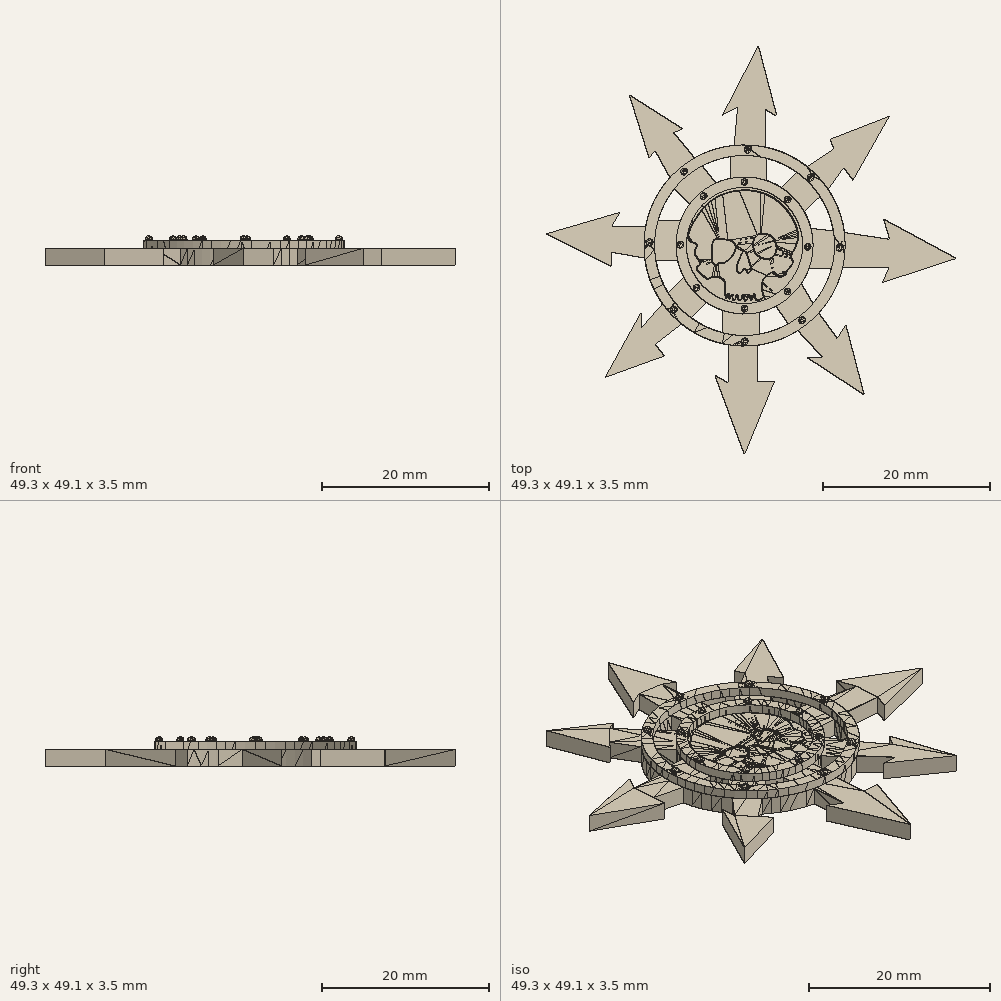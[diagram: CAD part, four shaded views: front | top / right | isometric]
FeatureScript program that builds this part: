
annotation { "Feature Type Name" : "Feature", "Feature Type Description" : "" }
export const myFeature = defineFeature(function(context is Context, id is Id, definition is map)
    precondition{}
    {
        {
            var Q0;
            Q0=qCreatedBy(makeId("Top.planeOp"),FACE);
            var sketch = newSketch(context, id + "F0", { "sketchPlane" : qUnion([Q0])});
            skLineSegment(sketch, "E0", {"start": v(0, -16.17) * mm, "end": v(-3.58, -6.6) * mm});
            skLineSegment(sketch, "E1", {"start": v(-3.58, -6.6) * mm, "end": v(-1.93, -7.54) * mm});
            skLineSegment(sketch, "E2", {"start": v(-1.93, -2.96) * mm, "end": v(-1.93, -2.93) * mm});
            skLineSegment(sketch, "E3", {"start": v(0, -16.17) * mm, "end": v(3.63, -7.3) * mm});
            skLineSegment(sketch, "E4", {"start": v(3.63, -7.3) * mm, "end": v(1.58, -7.3) * mm});
            skLineSegment(sketch, "E5", {"start": v(14.38, -8.95) * mm, "end": v(7.48, -4.44) * mm});
            skLineSegment(sketch, "E6", {"start": v(7.48, -4.44) * mm, "end": v(9.38, -4.44) * mm});
            skLineSegment(sketch, "E7", {"start": v(14.38, -8.95) * mm, "end": v(12.2, -0.6) * mm});
            skLineSegment(sketch, "E8", {"start": v(12.2, -0.6) * mm, "end": v(11.15, -2.18) * mm});
            skLineSegment(sketch, "E9", {"start": v(25.47, 7.44) * mm, "end": v(16.6, 4.54) * mm});
            skLineSegment(sketch, "E10", {"start": v(16.6, 4.54) * mm, "end": v(17.37, 6.37) * mm});
            skLineSegment(sketch, "E11", {"start": v(25.47, 7.44) * mm, "end": v(16.72, 12.17) * mm});
            skLineSegment(sketch, "E12", {"start": v(16.72, 12.17) * mm, "end": v(17.43, 9.74) * mm});
            skLineSegment(sketch, "E13", {"start": v(12.01, 10.56) * mm, "end": v(11.93, 10.57) * mm});
            skLineSegment(sketch, "E14", {"start": v(11.93, 18.31) * mm, "end": v(13.06, 16.84) * mm});
            skLineSegment(sketch, "E15", {"start": v(13.06, 16.84) * mm, "end": v(17.43, 24.52) * mm});
            skLineSegment(sketch, "E16", {"start": v(17.43, 24.52) * mm, "end": v(10.28, 21.74) * mm});
            skLineSegment(sketch, "E17", {"start": v(10.28, 21.74) * mm, "end": v(10.74, 20.55) * mm});
            skCircle(sketch, "E18", {"center": v(0, 9) * mm, "radius": 6.99 * mm});
            skArc(sketch, "E19", {"start": v(-6.58, 14) * mm, "mid": v(-7.21, 13.01) * mm, "end": v(-7.7, 11.95) * mm});
            skArc(sketch, "E20", {"start": v(-8.42, 15.76) * mm, "mid": v(-9.6, 13.96) * mm, "end": v(-10.38, 11.95) * mm});
            skArc(sketch, "E21", {"start": v(-1.24, 21.05) * mm, "mid": v(-3.7, 20.53) * mm, "end": v(-6, 19.52) * mm});
            skLineSegment(sketch, "E22", {"start": v(10.74, 20.55) * mm, "end": v(7.55, 18.47) * mm});
            skLineSegment(sketch, "E23", {"start": v(11.93, 18.31) * mm, "end": v(10.07, 15.73) * mm});
            skLineSegment(sketch, "E24", {"start": v(17.43, 9.74) * mm, "end": v(12.01, 10.56) * mm});
            skLineSegment(sketch, "E25", {"start": v(17.37, 6.37) * mm, "end": v(11.82, 6.37) * mm});
            skLineSegment(sketch, "E26", {"start": v(11.15, -2.18) * mm, "end": v(8.95, 0.84) * mm});
            skLineSegment(sketch, "E27", {"start": v(9.38, -4.44) * mm, "end": v(6.43, -1.26) * mm});
            skLineSegment(sketch, "E28", {"start": v(1.58, -7.3) * mm, "end": v(1.58, -3) * mm});
            skLineSegment(sketch, "E29", {"start": v(-1.93, -7.54) * mm, "end": v(-1.93, -2.96) * mm});
            skLineSegment(sketch, "E30", {"start": v(-9.85, 1.95) * mm, "end": v(-12.42, -0.96) * mm});
            skLineSegment(sketch, "E31", {"start": v(-12.42, -0.96) * mm, "end": v(-12.42, 0.93) * mm});
            skLineSegment(sketch, "E32", {"start": v(-12.42, 0.93) * mm, "end": v(-16.74, -6.87) * mm});
            skLineSegment(sketch, "E33", {"start": v(-16.74, -6.87) * mm, "end": v(-9.63, -4.3) * mm});
            skLineSegment(sketch, "E34", {"start": v(-9.63, -4.3) * mm, "end": v(-10.7, -2.92) * mm});
            skLineSegment(sketch, "E35", {"start": v(-10.7, -2.92) * mm, "end": v(-7.57, -0.46) * mm});
            skLineSegment(sketch, "E36", {"start": v(-12.02, 7.5) * mm, "end": v(-15.95, 8.18) * mm});
            skLineSegment(sketch, "E37", {"start": v(-15.95, 8.18) * mm, "end": v(-15.95, 6.43) * mm});
            skLineSegment(sketch, "E38", {"start": v(-15.95, 6.43) * mm, "end": v(-23.8, 10.4) * mm});
            skLineSegment(sketch, "E39", {"start": v(-23.8, 10.4) * mm, "end": v(-14.94, 12.98) * mm});
            skLineSegment(sketch, "E40", {"start": v(-14.94, 12.98) * mm, "end": v(-15.98, 11.23) * mm});
            skLineSegment(sketch, "E41", {"start": v(-15.98, 11.23) * mm, "end": v(-11.9, 11.23) * mm});
            skLineSegment(sketch, "E42", {"start": v(-8.97, 17.14) * mm, "end": v(-10.73, 20.34) * mm});
            skLineSegment(sketch, "E43", {"start": v(-10.73, 20.34) * mm, "end": v(-11.47, 19.5) * mm});
            skLineSegment(sketch, "E44", {"start": v(-11.47, 19.5) * mm, "end": v(-13.86, 27.1) * mm});
            skLineSegment(sketch, "E45", {"start": v(-13.86, 27.1) * mm, "end": v(-7.45, 23.03) * mm});
            skLineSegment(sketch, "E46", {"start": v(-7.45, 23.03) * mm, "end": v(-8.49, 22.53) * mm});
            skLineSegment(sketch, "E47", {"start": v(-8.49, 22.53) * mm, "end": v(-6, 19.52) * mm});
            skLineSegment(sketch, "E48", {"start": v(-1.24, 21.05) * mm, "end": v(-0.83, 25.6) * mm});
            skLineSegment(sketch, "E49", {"start": v(-0.83, 25.6) * mm, "end": v(-2.62, 24.67) * mm});
            skLineSegment(sketch, "E50", {"start": v(-2.62, 24.67) * mm, "end": v(1.67, 32.98) * mm});
            skLineSegment(sketch, "E51", {"start": v(1.67, 32.98) * mm, "end": v(3.89, 24.53) * mm});
            skLineSegment(sketch, "E52", {"start": v(3.89, 24.53) * mm, "end": v(2.52, 25.33) * mm});
            skLineSegment(sketch, "E53", {"start": v(2.52, 25.33) * mm, "end": v(2.52, 20.85) * mm});
            skArc(sketch, "E54.trimOffspring", {"start": v(-8.97, 17.14) * mm, "mid": v(-10.85, 14.4) * mm, "end": v(-11.9, 11.23) * mm});
            skArc(sketch, "E55.trimOffspring", {"start": v(7.55, 18.47) * mm, "mid": v(5.17, 19.95) * mm, "end": v(2.52, 20.85) * mm});
            skArc(sketch, "E56.trimOffspring", {"start": v(12.01, 10.56) * mm, "mid": v(11.34, 13.26) * mm, "end": v(10.07, 15.73) * mm});
            skArc(sketch, "E57.trimOffspring", {"start": v(-12.02, 7.5) * mm, "mid": v(-11.28, 4.59) * mm, "end": v(-9.85, 1.95) * mm});
            skArc(sketch, "E58.trimOffspring", {"start": v(8.95, 0.84) * mm, "mid": v(10.75, 3.42) * mm, "end": v(11.82, 6.37) * mm});
            skArc(sketch, "E59.trimOffspring", {"start": v(1.58, -3) * mm, "mid": v(4.1, -2.4) * mm, "end": v(6.43, -1.26) * mm});
            skArc(sketch, "E60.trimOffspring", {"start": v(-7.57, -0.46) * mm, "mid": v(-4.9, -2.07) * mm, "end": v(-1.93, -2.96) * mm});
            skLineSegment(sketch, "E61", {"start": v(-1.64, 19.67) * mm, "end": v(-1.64, 17.1) * mm});
            skLineSegment(sketch, "E62", {"start": v(2.69, 19.46) * mm, "end": v(2.69, 16.8) * mm});
            skLineSegment(sketch, "E63", {"start": v(6.26, 17.8) * mm, "end": v(4.47, 15.94) * mm});
            skLineSegment(sketch, "E64", {"start": v(9.08, 14.83) * mm, "end": v(7.19, 13.06) * mm});
            skLineSegment(sketch, "E65", {"start": v(10.65, 10.75) * mm, "end": v(8, 11.06) * mm});
            skLineSegment(sketch, "E66", {"start": v(10.44, 6.24) * mm, "end": v(7.78, 6.24) * mm});
            skLineSegment(sketch, "E67", {"start": v(8.24, 2.02) * mm, "end": v(6.84, 4.37) * mm});
            skLineSegment(sketch, "E68", {"start": v(5.25, -0.43) * mm, "end": v(3.8, 1.67) * mm});
            skLineSegment(sketch, "E69", {"start": v(1.82, -1.64) * mm, "end": v(1.82, 0.95) * mm});
            skLineSegment(sketch, "E70", {"start": v(-2.6, -1.48) * mm, "end": v(-2.6, 1.17) * mm});
            skLineSegment(sketch, "E71", {"start": v(-6.4, 0.3) * mm, "end": v(-4.52, 2.1) * mm});
            skLineSegment(sketch, "E72", {"start": v(-9.17, 3.3) * mm, "end": v(-7.3, 5.14) * mm});
            skLineSegment(sketch, "E73", {"start": v(-10.64, 7.16) * mm, "end": v(-8.05, 7.16) * mm});
            skLineSegment(sketch, "E74", {"start": v(-10.38, 11.95) * mm, "end": v(-7.7, 11.95) * mm});
            skLineSegment(sketch, "E75", {"start": v(-8.42, 15.76) * mm, "end": v(-6.58, 14) * mm});
            skLineSegment(sketch, "E76", {"start": v(-5.07, 18.53) * mm, "end": v(-3.44, 16.5) * mm});
            skArc(sketch, "E77.trimOffspring", {"start": v(-8.05, 7.16) * mm, "mid": v(-7.74, 6.13) * mm, "end": v(-7.3, 5.14) * mm});
            skArc(sketch, "E78.trimOffspring", {"start": v(-4.52, 2.1) * mm, "mid": v(-3.6, 1.57) * mm, "end": v(-2.6, 1.17) * mm});
            skArc(sketch, "E79.trimOffspring", {"start": v(-6.4, 0.3) * mm, "mid": v(-4.59, -0.77) * mm, "end": v(-2.6, -1.48) * mm});
            skArc(sketch, "E80.trimOffspring", {"start": v(-10.64, 7.16) * mm, "mid": v(-10.09, 5.16) * mm, "end": v(-9.17, 3.3) * mm});
            skArc(sketch, "E81.trimOffspring", {"start": v(-1.64, 19.67) * mm, "mid": v(-3.4, 19.25) * mm, "end": v(-5.07, 18.53) * mm});
            skArc(sketch, "E82.trimOffspring", {"start": v(-1.64, 17.1) * mm, "mid": v(-2.56, 16.85) * mm, "end": v(-3.44, 16.5) * mm});
            skArc(sketch, "E83.trimOffspring", {"start": v(4.47, 15.94) * mm, "mid": v(3.6, 16.43) * mm, "end": v(2.69, 16.8) * mm});
            skArc(sketch, "E84.trimOffspring", {"start": v(6.26, 17.8) * mm, "mid": v(4.55, 18.8) * mm, "end": v(2.69, 19.46) * mm});
            skArc(sketch, "E85.trimOffspring", {"start": v(10.65, 10.75) * mm, "mid": v(10.08, 12.87) * mm, "end": v(9.08, 14.83) * mm});
            skArc(sketch, "E86.trimOffspring", {"start": v(8, 11.06) * mm, "mid": v(7.66, 12.09) * mm, "end": v(7.19, 13.06) * mm});
            skArc(sketch, "E87.trimOffspring", {"start": v(8.24, 2.02) * mm, "mid": v(9.57, 4) * mm, "end": v(10.44, 6.24) * mm});
            skArc(sketch, "E88.trimOffspring", {"start": v(6.84, 4.37) * mm, "mid": v(7.37, 5.28) * mm, "end": v(7.78, 6.24) * mm});
            skArc(sketch, "E89.trimOffspring", {"start": v(1.82, 0.95) * mm, "mid": v(2.83, 1.25) * mm, "end": v(3.8, 1.67) * mm});
            skArc(sketch, "E90.trimOffspring", {"start": v(1.82, -1.64) * mm, "mid": v(3.59, -1.18) * mm, "end": v(5.25, -0.43) * mm});
            skCircle(sketch, "E91", {"center": v(0, 9) * mm, "radius": 8.24 * mm});
            skCircle(sketch, "E92", {"center": v(0, 9) * mm, "radius": 12.1 * mm});
            skCircle(sketch, "E93", {"center": v(0, 9) * mm, "radius": 10.82 * mm});
            skSolve(sketch);
        }
        {
            var Q0;
            Q0 = qSketchRegion(id + "F0", true);
            extrude(context, id + "F1", {"entities" : qUnion([Q0]), "depth" : 2 * mm});
        }
        {
            var Q0;
            Q0=makeQuery(id+"F0.imprint","IMPRINT",FACE,{"disambiguationData":[TD([[makeQuery(id+"F0.imprint","IMPRINT",EDGE,{"derivedFrom":sQuery(id+"F0.wireOp",EDGE,"E18")}),1.0]])]});
            extrude(context, id + "F2", {"entities" : qUnion([Q0]), "operationType" : NewBodyOperationType.ADD, "depth" : 2 * mm});
        }
        {
            var Q0;
            Q0=makeQuery(id+"F0.imprint","IMPRINT",FACE,{"disambiguationData":[TD([[makeQuery(id+"F0.imprint","IMPRINT",EDGE,{"derivedFrom":sQuery(id+"F0.wireOp",EDGE,"E19")}),1.0]])]});
            extrude(context, id + "F3", {"entities" : qUnion([Q0]), "operationType" : NewBodyOperationType.ADD, "depth" : 2 * mm});
        }
        {
            var Q0;
            Q0=makeQuery(id+"F0.imprint","IMPRINT",FACE,{"disambiguationData":[TD([[makeQuery(id+"F0.imprint","IMPRINT",EDGE,{"derivedFrom":sQuery(id+"F0.wireOp",EDGE,"E18")}),-1.0]])]});
            var Q1;
            Q1=makeQuery(id+"F0.imprint","IMPRINT",FACE,{"disambiguationData":[TD([[makeQuery(id+"F0.imprint","IMPRINT",EDGE,{"derivedFrom":sQuery(id+"F0.wireOp",EDGE,"E93")}),-1.0]])]});
            extrude(context, id + "F4", {"entities" : qUnion([Q0, Q1]), "depth" : 3 * mm});
        }
        {
            var Q0;
            Q0=makeQuery(id+"F2.opExtrude","CAP_FACE",FACE,{"disambiguationData":[OSD([sQuery(id+"F0.wireOp",EDGE,"E18")])],"isStart":false});
            var sketch = newSketch(context, id + "F5", { "sketchPlane" : qUnion([Q0])});
            skFitSpline(sketch, "E94", {"points": [v(-3.63, 9.6) * mm, v(-2.74, 9.72) * mm, v(-1.66, 9.54) * mm, v(-1.14, 8.98) * mm, v(-1.26, 8.15) * mm, v(-1.72, 7.5) * mm, v(-2.62, 6.92) * mm, v(-3.14, 6.92) * mm, v(-3.26, 6.67) * mm, v(-3.76, 6.92) * mm, v(-3.88, 7.72) * mm, v(-3.63, 9.6) * mm]});
            skFitSpline(sketch, "E95", {"points": [v(1.51, 10.16) * mm, v(2.68, 10.3) * mm, v(3.58, 9.6) * mm, v(3.7, 8.12) * mm, v(2.96, 7.44) * mm, v(1.64, 7.81) * mm, v(1.08, 8.95) * mm, v(1.51, 10.16) * mm]});
            skFitSpline(sketch, "E96", {"points": [v(-0.46, 5.75) * mm, v(-0.86, 5.96) * mm, v(-0.74, 6.92) * mm, v(-0.37, 7.78) * mm, v(0, 8.24) * mm, v(0.5, 7.17) * mm, v(0.71, 5.96) * mm, v(0.43, 5.78) * mm, v(0, 6.3) * mm, v(-0.46, 5.75) * mm]});
            skFitSpline(sketch, "E97", {"points": [v(-4.46, 4.87) * mm, v(-3.63, 5.17) * mm, v(-2.62, 4.87) * mm, v(-2.38, 4.31) * mm, v(-2.4, 3.38) * mm, v(-2.14, 2.6) * mm, v(-1.96, 3.14) * mm, v(-1.8, 2.53) * mm, v(-1.48, 3.06) * mm, v(-1.47, 2.55) * mm, v(-1.11, 2.46) * mm, v(-0.9, 3.04) * mm, v(-0.74, 2.43) * mm, v(-0.37, 2.46) * mm, v(-0.2, 3.06) * mm, v(0, 2.35) * mm, v(0.35, 2.44) * mm, v(0.51, 3.04) * mm, v(0.83, 2.35) * mm, v(1.17, 3.09) * mm, v(1.37, 2.45) * mm, v(2.3, 2.72) * mm, v(2.27, 3.14) * mm, v(2.22, 4.68) * mm, v(3.3, 5.7) * mm], "startDerivative": vector(16.77, 9.14) * mm, "endDerivative": vector(23.15, 14.13) * mm});
            skFitSpline(sketch, "E98", {"points": [v(3.3, 5.7) * mm, v(3.55, 5.7) * mm, v(4.1, 5.2) * mm, v(4.99, 5.46) * mm, v(5.05, 5.7) * mm, v(5.87, 6.97) * mm, v(5.64, 7.55) * mm, v(6.46, 9.68) * mm, v(4.43, 14.02) * mm, v(0.42, 15.69) * mm, v(-3.37, 14.8) * mm, v(-5.85, 12.29) * mm, v(-6.7, 9.61) * mm, v(-5.75, 9.06) * mm, v(-6.05, 8.1) * mm, v(-5.36, 6.84) * mm, v(-5.79, 6.35) * mm, v(-4.46, 4.87) * mm], "startDerivative": vector(10.94, 3.43) * mm, "endDerivative": vector(33.26, -26.4) * mm});
            skSolve(sketch);
        }
        {
            var Q0;
            Q0=makeQuery(id+"F5.imprint","IMPRINT",FACE,{"disambiguationData":[TD([[makeQuery(id+"F5.imprint","IMPRINT",EDGE,{"derivedFrom":sQuery(id+"F5.wireOp",EDGE,"E94")}),1.0]])]});
            extrude(context, id + "F6", {"entities" : qUnion([Q0]), "operationType" : NewBodyOperationType.ADD, "depth" : .2 * mm});
        }
        {
            var Q0;
            Q0=makeQuery(id+"F6.opExtrude","CAP_EDGE",EDGE,{"disambiguationData":[OSD([sQuery(id+"F5.wireOp",EDGE,"E94")])],"isStart":false});
            fillet(context, id + "F7", {"entities" : qUnion([Q0]), "radius" : .1 * mm, "tangentPropagation" : true, "allowEdgeOverflow" : false});
        }
        {
            var Q0;
            Q0=makeQuery(id+"F6.opExtrude","CAP_EDGE",EDGE,{"disambiguationData":[OSD([sQuery(id+"F5.wireOp",EDGE,"E95")])],"isStart":false});
            var Q1;
            Q1=makeQuery(id+"F6.opExtrude","CAP_FACE",FACE,{"disambiguationData":[OSD([sQuery(id+"F5.wireOp",EDGE,"E94"),sQuery(id+"F5.wireOp",EDGE,"E95"),sQuery(id+"F5.wireOp",EDGE,"E96"),sQuery(id+"F5.wireOp",EDGE,"E97"),sQuery(id+"F5.wireOp",EDGE,"E98")])],"isStart":false});
            fillet(context, id + "F8", {"entities" : qUnion([Q0, Q1]), "radius" : .1 * mm, "tangentPropagation" : true, "allowEdgeOverflow" : false});
        }
        {
            var Q0;
            Q0=makeQuery(id+"F4.opExtrude","CAP_FACE",FACE,{"disambiguationData":[OSD([sQuery(id+"F0.wireOp",EDGE,"E92"),sQuery(id+"F0.wireOp",EDGE,"E93")])],"isStart":false});
            var sketch = newSketch(context, id + "F9", { "sketchPlane" : qUnion([Q0])});
            skCircle(sketch, "E99", {"center": v(-11.4, 9.38) * mm, "radius": 0.42 * mm});
            skCircle(sketch, "E100", {"center": v(-8.5, 1.27) * mm, "radius": 0.42 * mm});
            skCircle(sketch, "E101", {"center": v(0, -2.53) * mm, "radius": 0.42 * mm});
            skCircle(sketch, "E102", {"center": v(6.94, 0) * mm, "radius": 0.42 * mm});
            skCircle(sketch, "E103", {"center": v(11.44, 8.72) * mm, "radius": 0.42 * mm});
            skCircle(sketch, "E104", {"center": v(7.95, 17.16) * mm, "radius": 0.42 * mm});
            skCircle(sketch, "E105", {"center": v(0.4, 20.5) * mm, "radius": 0.42 * mm});
            skCircle(sketch, "E106", {"center": v(-7.22, 17.9) * mm, "radius": 0.42 * mm});
            skSolve(sketch);
        }
        {
            var Q0;
            Q0=makeQuery(id+"F9.imprint","IMPRINT",FACE,{"disambiguationData":[TD([[makeQuery(id+"F9.imprint","IMPRINT",EDGE,{"derivedFrom":sQuery(id+"F9.wireOp",EDGE,"E100")}),1.0]])]});
            var Q1;
            Q1=makeQuery(id+"F9.imprint","IMPRINT",FACE,{"disambiguationData":[TD([[makeQuery(id+"F9.imprint","IMPRINT",EDGE,{"derivedFrom":sQuery(id+"F9.wireOp",EDGE,"E101")}),1.0]])]});
            var Q2;
            Q2=makeQuery(id+"F9.imprint","IMPRINT",FACE,{"disambiguationData":[TD([[makeQuery(id+"F9.imprint","IMPRINT",EDGE,{"derivedFrom":sQuery(id+"F9.wireOp",EDGE,"E102")}),1.0]])]});
            var Q3;
            Q3=makeQuery(id+"F9.imprint","IMPRINT",FACE,{"disambiguationData":[TD([[makeQuery(id+"F9.imprint","IMPRINT",EDGE,{"derivedFrom":sQuery(id+"F9.wireOp",EDGE,"E103")}),1.0]])]});
            var Q4;
            Q4=makeQuery(id+"F9.imprint","IMPRINT",FACE,{"disambiguationData":[TD([[makeQuery(id+"F9.imprint","IMPRINT",EDGE,{"derivedFrom":sQuery(id+"F9.wireOp",EDGE,"E104")}),1.0]])]});
            var Q5;
            Q5=makeQuery(id+"F9.imprint","IMPRINT",FACE,{"disambiguationData":[TD([[makeQuery(id+"F9.imprint","IMPRINT",EDGE,{"derivedFrom":sQuery(id+"F9.wireOp",EDGE,"E105")}),1.0]])]});
            var Q6;
            Q6=makeQuery(id+"F9.imprint","IMPRINT",FACE,{"disambiguationData":[TD([[makeQuery(id+"F9.imprint","IMPRINT",EDGE,{"derivedFrom":sQuery(id+"F9.wireOp",EDGE,"E106")}),1.0]])]});
            var Q7;
            Q7=makeQuery(id+"F9.imprint","IMPRINT",FACE,{"disambiguationData":[TD([[makeQuery(id+"F9.imprint","IMPRINT",EDGE,{"derivedFrom":sQuery(id+"F9.wireOp",EDGE,"E99")}),1.0]])]});
            extrude(context, id + "F10", {"entities" : qUnion([Q0, Q1, Q2, Q3, Q4, Q5, Q6, Q7]), "operationType" : NewBodyOperationType.ADD, "depth" : .5 * mm});
        }
        {
            var Q0;
            Q0=makeQuery(id+"F10.opExtrude","CAP_EDGE",EDGE,{"disambiguationData":[OSD([sQuery(id+"F9.wireOp",EDGE,"E99")])],"isStart":false});
            fillet(context, id + "F11", {"entities" : qUnion([Q0]), "radius" : .4 * mm, "tangentPropagation" : true, "allowEdgeOverflow" : false});
        }
        {
            var Q0;
            Q0=makeQuery(id+"F10.opExtrude","CAP_EDGE",EDGE,{"disambiguationData":[OSD([sQuery(id+"F9.wireOp",EDGE,"E106")])],"isStart":false});
            var Q1;
            Q1=makeQuery(id+"F10.opExtrude","CAP_EDGE",EDGE,{"disambiguationData":[OSD([sQuery(id+"F9.wireOp",EDGE,"E100")])],"isStart":false});
            var Q2;
            Q2=makeQuery(id+"F10.opExtrude","CAP_EDGE",EDGE,{"disambiguationData":[OSD([sQuery(id+"F9.wireOp",EDGE,"E101")])],"isStart":false});
            var Q3;
            Q3=makeQuery(id+"F10.opExtrude","CAP_EDGE",EDGE,{"disambiguationData":[OSD([sQuery(id+"F9.wireOp",EDGE,"E102")])],"isStart":false});
            var Q4;
            Q4=makeQuery(id+"F10.opExtrude","CAP_EDGE",EDGE,{"disambiguationData":[OSD([sQuery(id+"F9.wireOp",EDGE,"E105")])],"isStart":false});
            var Q5;
            Q5=makeQuery(id+"F10.opExtrude","CAP_EDGE",EDGE,{"disambiguationData":[OSD([sQuery(id+"F9.wireOp",EDGE,"E104")])],"isStart":false});
            var Q6;
            Q6=makeQuery(id+"F10.opExtrude","CAP_EDGE",EDGE,{"disambiguationData":[OSD([sQuery(id+"F9.wireOp",EDGE,"E103")])],"isStart":false});
            fillet(context, id + "F12", {"entities" : qUnion([Q0, Q1, Q2, Q3, Q4, Q5, Q6]), "radius" : .4 * mm, "tangentPropagation" : true, "allowEdgeOverflow" : false});
        }
        {
            var Q0;
            Q0=makeQuery(id+"F4.opExtrude","CAP_FACE",FACE,{"disambiguationData":[OSD([sQuery(id+"F0.wireOp",EDGE,"E18"),sQuery(id+"F0.wireOp",EDGE,"E91")])],"isStart":false});
            var sketch = newSketch(context, id + "F13", { "sketchPlane" : qUnion([Q0])});
            skCircle(sketch, "E107", {"center": v(0, 16.63) * mm, "radius": 0.4 * mm});
            skCircle(sketch, "E108", {"center": v(5.2, 14.51) * mm, "radius": 0.4 * mm});
            skCircle(sketch, "E109", {"center": v(-4.9, 14.92) * mm, "radius": 0.4 * mm});
            skCircle(sketch, "E110", {"center": v(-7.7, 9.08) * mm, "radius": 0.4 * mm});
            skCircle(sketch, "E111", {"center": v(-5.76, 3.9) * mm, "radius": 0.4 * mm});
            skCircle(sketch, "E112", {"center": v(7.59, 8.82) * mm, "radius": 0.4 * mm});
            skCircle(sketch, "E113", {"center": v(5.18, 3.45) * mm, "radius": 0.4 * mm});
            skCircle(sketch, "E114", {"center": v(0, 1.4) * mm, "radius": 0.4 * mm});
            skSolve(sketch);
        }
        {
            var Q0;
            Q0 = qSketchRegion(id + "F13", true);
            extrude(context, id + "F14", {"entities" : qUnion([Q0]), "operationType" : NewBodyOperationType.ADD, "depth" : .5 * mm});
        }
        {
            var Q0;
            Q0=makeQuery(id+"F14.opExtrude","CAP_EDGE",EDGE,{"disambiguationData":[OSD([sQuery(id+"F13.wireOp",EDGE,"E109")])],"isStart":false});
            var Q1;
            Q1=makeQuery(id+"F14.opExtrude","CAP_EDGE",EDGE,{"disambiguationData":[OSD([sQuery(id+"F13.wireOp",EDGE,"E110")])],"isStart":false});
            var Q2;
            Q2=makeQuery(id+"F14.opExtrude","CAP_EDGE",EDGE,{"disambiguationData":[OSD([sQuery(id+"F13.wireOp",EDGE,"E111")])],"isStart":false});
            var Q3;
            Q3=makeQuery(id+"F14.opExtrude","CAP_EDGE",EDGE,{"disambiguationData":[OSD([sQuery(id+"F13.wireOp",EDGE,"E114")])],"isStart":false});
            var Q4;
            Q4=makeQuery(id+"F14.opExtrude","CAP_EDGE",EDGE,{"disambiguationData":[OSD([sQuery(id+"F13.wireOp",EDGE,"E113")])],"isStart":false});
            var Q5;
            Q5=makeQuery(id+"F14.opExtrude","CAP_EDGE",EDGE,{"disambiguationData":[OSD([sQuery(id+"F13.wireOp",EDGE,"E112")])],"isStart":false});
            var Q6;
            Q6=makeQuery(id+"F14.opExtrude","CAP_EDGE",EDGE,{"disambiguationData":[OSD([sQuery(id+"F13.wireOp",EDGE,"E108")])],"isStart":false});
            var Q7;
            Q7=makeQuery(id+"F14.opExtrude","CAP_EDGE",EDGE,{"disambiguationData":[OSD([sQuery(id+"F13.wireOp",EDGE,"E107")])],"isStart":false});
            fillet(context, id + "F15", {"entities" : qUnion([Q0, Q1, Q2, Q3, Q4, Q5, Q6, Q7]), "radius" : .4 * mm, "tangentPropagation" : true, "allowEdgeOverflow" : false});
        }
        {
            var Q0;
            Q0=makeQuery(id+"F4.opExtrude","SWEPT_BODY",BODY,{"disambiguationData":[OSD([sQuery(id+"F0.wireOp",EDGE,"E92"),sQuery(id+"F0.wireOp",EDGE,"E93")])]});
            var Q1;
            Q1=makeQuery(id+"F4.opExtrude","SWEPT_BODY",BODY,{"disambiguationData":[OSD([sQuery(id+"F0.wireOp",EDGE,"E18"),sQuery(id+"F0.wireOp",EDGE,"E91")])]});
            var Q2;
            Q2=makeQuery(id+"F3.opExtrude","SWEPT_BODY",BODY,{"disambiguationData":[OSD([sQuery(id+"F0.wireOp",EDGE,"E19"),sQuery(id+"F0.wireOp",EDGE,"E20"),sQuery(id+"F0.wireOp",EDGE,"E61"),sQuery(id+"F0.wireOp",EDGE,"E62"),sQuery(id+"F0.wireOp",EDGE,"E63"),sQuery(id+"F0.wireOp",EDGE,"E64"),sQuery(id+"F0.wireOp",EDGE,"E65"),sQuery(id+"F0.wireOp",EDGE,"E66"),sQuery(id+"F0.wireOp",EDGE,"E67"),sQuery(id+"F0.wireOp",EDGE,"E68"),sQuery(id+"F0.wireOp",EDGE,"E69"),sQuery(id+"F0.wireOp",EDGE,"E70"),sQuery(id+"F0.wireOp",EDGE,"E71"),sQuery(id+"F0.wireOp",EDGE,"E72"),sQuery(id+"F0.wireOp",EDGE,"E73"),sQuery(id+"F0.wireOp",EDGE,"E74"),sQuery(id+"F0.wireOp",EDGE,"E75"),sQuery(id+"F0.wireOp",EDGE,"E76"),sQuery(id+"F0.wireOp",EDGE,"E77.trimOffspring"),sQuery(id+"F0.wireOp",EDGE,"E78.trimOffspring"),sQuery(id+"F0.wireOp",EDGE,"E79.trimOffspring"),sQuery(id+"F0.wireOp",EDGE,"E80.trimOffspring"),sQuery(id+"F0.wireOp",EDGE,"E81.trimOffspring"),sQuery(id+"F0.wireOp",EDGE,"E82.trimOffspring"),sQuery(id+"F0.wireOp",EDGE,"E83.trimOffspring"),sQuery(id+"F0.wireOp",EDGE,"E84.trimOffspring"),sQuery(id+"F0.wireOp",EDGE,"E85.trimOffspring"),sQuery(id+"F0.wireOp",EDGE,"E86.trimOffspring"),sQuery(id+"F0.wireOp",EDGE,"E87.trimOffspring"),sQuery(id+"F0.wireOp",EDGE,"E88.trimOffspring"),sQuery(id+"F0.wireOp",EDGE,"E89.trimOffspring"),sQuery(id+"F0.wireOp",EDGE,"E90.trimOffspring"),sQuery(id+"F0.wireOp",EDGE,"E91"),sQuery(id+"F0.wireOp",EDGE,"E93")])]});
            var Q3;
            Q3=makeQuery(id+"F2.opExtrude","SWEPT_BODY",BODY,{"disambiguationData":[OSD([sQuery(id+"F0.wireOp",EDGE,"E18")])]});
            var Q4;
            Q4=makeQuery(id+"F1.opExtrude","SWEPT_BODY",BODY,{"disambiguationData":[OSD([sQuery(id+"F0.wireOp",EDGE,"E0"),sQuery(id+"F0.wireOp",EDGE,"E1"),sQuery(id+"F0.wireOp",EDGE,"E3"),sQuery(id+"F0.wireOp",EDGE,"E4"),sQuery(id+"F0.wireOp",EDGE,"E5"),sQuery(id+"F0.wireOp",EDGE,"E6"),sQuery(id+"F0.wireOp",EDGE,"E7"),sQuery(id+"F0.wireOp",EDGE,"E8"),sQuery(id+"F0.wireOp",EDGE,"E9"),sQuery(id+"F0.wireOp",EDGE,"E10"),sQuery(id+"F0.wireOp",EDGE,"E11"),sQuery(id+"F0.wireOp",EDGE,"E12"),sQuery(id+"F0.wireOp",EDGE,"E14"),sQuery(id+"F0.wireOp",EDGE,"E15"),sQuery(id+"F0.wireOp",EDGE,"E16"),sQuery(id+"F0.wireOp",EDGE,"E17"),sQuery(id+"F0.wireOp",EDGE,"E21"),sQuery(id+"F0.wireOp",EDGE,"E22"),sQuery(id+"F0.wireOp",EDGE,"E23"),sQuery(id+"F0.wireOp",EDGE,"E24"),sQuery(id+"F0.wireOp",EDGE,"E25"),sQuery(id+"F0.wireOp",EDGE,"E26"),sQuery(id+"F0.wireOp",EDGE,"E27"),sQuery(id+"F0.wireOp",EDGE,"E28"),sQuery(id+"F0.wireOp",EDGE,"E29"),sQuery(id+"F0.wireOp",EDGE,"E30"),sQuery(id+"F0.wireOp",EDGE,"E31"),sQuery(id+"F0.wireOp",EDGE,"E32"),sQuery(id+"F0.wireOp",EDGE,"E33"),sQuery(id+"F0.wireOp",EDGE,"E34"),sQuery(id+"F0.wireOp",EDGE,"E35"),sQuery(id+"F0.wireOp",EDGE,"E36"),sQuery(id+"F0.wireOp",EDGE,"E37"),sQuery(id+"F0.wireOp",EDGE,"E38"),sQuery(id+"F0.wireOp",EDGE,"E39"),sQuery(id+"F0.wireOp",EDGE,"E40"),sQuery(id+"F0.wireOp",EDGE,"E41"),sQuery(id+"F0.wireOp",EDGE,"E42"),sQuery(id+"F0.wireOp",EDGE,"E43"),sQuery(id+"F0.wireOp",EDGE,"E44"),sQuery(id+"F0.wireOp",EDGE,"E45"),sQuery(id+"F0.wireOp",EDGE,"E46"),sQuery(id+"F0.wireOp",EDGE,"E47"),sQuery(id+"F0.wireOp",EDGE,"E48"),sQuery(id+"F0.wireOp",EDGE,"E49"),sQuery(id+"F0.wireOp",EDGE,"E50"),sQuery(id+"F0.wireOp",EDGE,"E51"),sQuery(id+"F0.wireOp",EDGE,"E52"),sQuery(id+"F0.wireOp",EDGE,"E53"),sQuery(id+"F0.wireOp",EDGE,"E54.trimOffspring"),sQuery(id+"F0.wireOp",EDGE,"E55.trimOffspring"),sQuery(id+"F0.wireOp",EDGE,"E56.trimOffspring"),sQuery(id+"F0.wireOp",EDGE,"E57.trimOffspring"),sQuery(id+"F0.wireOp",EDGE,"E58.trimOffspring"),sQuery(id+"F0.wireOp",EDGE,"E59.trimOffspring"),sQuery(id+"F0.wireOp",EDGE,"E60.trimOffspring"),sQuery(id+"F0.wireOp",EDGE,"E92")])]});
            var Q5;
            Q5=sQuery(id+"F0.wireOp",VERTEX,"E88.trimOffspring.center");
            transform(context, id + "F16", {"entities" : qUnion([Q0, Q1, Q2, Q3, Q4]), "transformType" : TransformType.COPY});
        }
    });
